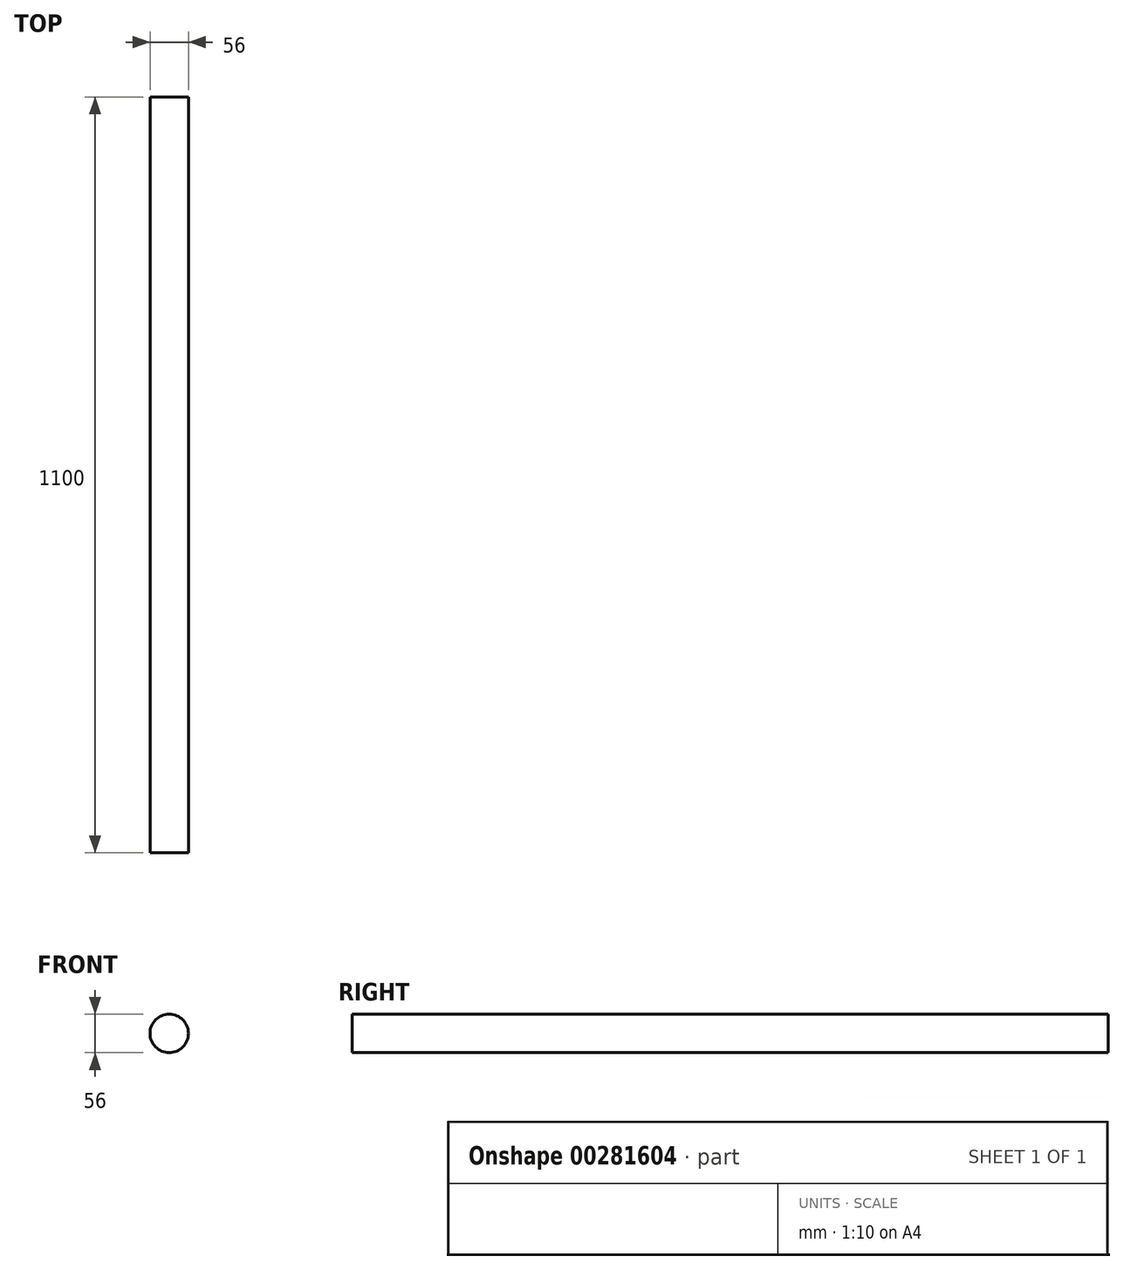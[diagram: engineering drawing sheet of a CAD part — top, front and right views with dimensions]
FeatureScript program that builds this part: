
annotation { "Feature Type Name" : "Feature", "Feature Type Description" : "" }
export const myFeature = defineFeature(function(context is Context, id is Id, definition is map)
    precondition{}
    {
        {
            var Q0;
            Q0=qCreatedBy(makeId("Front.planeOp"), FACE);
            var sketch = newSketch(context, id + "F0", { "sketchPlane" : qUnion([Q0])});
            skCircle(sketch, "E0", {"center": v(0, 0) * mm, "radius": 28 * mm});
            skSolve(sketch);
        }
        {
            var Q0;
            Q0 = qSketchRegion(id + "F0", true);
            extrude(context, id + "F1", {"entities" : qUnion([Q0]), "depth" : 1100 * mm, "offsetDistance" : 25 * mm});
        }
    });
